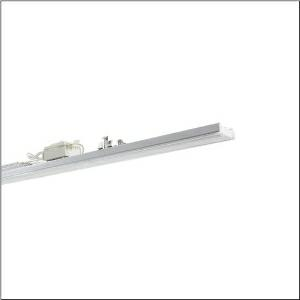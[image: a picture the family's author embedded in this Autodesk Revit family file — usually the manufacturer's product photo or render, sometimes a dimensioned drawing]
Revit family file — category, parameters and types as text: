
# Revit family: licross_r__11_recessed_ho_51tl12dn6d5m_dd4d
name_source: partatom
category: Lighting Fixtures
units: mm (PartAtom-declared; Revit-internal decimal feet)

## family parameters
Cut with Voids When Loaded = No
Host = Face
Light Source = No
Part Type = Normal
Room Calculation Point = No
Round Connector Dimension = Use Diameter
Shared = No

## types (1)
- --- (1 x LED, 13710 lm, 76.8 W, 6500K)
    Apparent Load = 77 VA
    CIE Flux Codes = 66 91 98 100 100
    Color Rendering = 80
    Color Temperature = 6500K
    Default Elevation = 1800 mm
    Description = Licross® 11 Recessed HO, luminaire insert, of sheet steel, coil coated, white, length: 1.500mm, width: 66mm, height: 67mm, LED rated luminous flux: 13.710lm, light colour: 865, control gear: DALI 2, with plug, 5-pole, with phase selection, mains connection: 220..240V, AC, 50/60Hz, rated input power: 77W, internal wiring halogen-free, primary optical cover: cover, of PMMA, light emission: direct distribution, primary light characteristic: symmetric, protection rating (complete): IP40, insulation class (complete): insulation class I (protective earthing), certification: CE, ENEC, VDE, UKCA, protection symbol: D if used in an environment without relevant dust loads with corresponding accessories, impact resistance: IK06, permissible ambient temperature for indoor applications: -25..+30°C, corresponds to IFS (International Featured Standards) requirements for safety and quality in the food industry, reducing of maximum allowable ambient temperature of 5°C with ceiling mounting, LABS conformity tested according to VDMA 24364:2018-05, packaging unit: 1 piece
    Height = 58 mm
    Lamp = 1 x LED
    Lamp Light Flux = 13710 lm
    Lamp Power = 76.8 W
    Lamp count = 1
    Length = 1500 mm
    Luminous efficacy = 179 lm/W
    Manufacturer = Siteco
    ModVariant = No
    Model = 51TL12DN6D5M
    Mounting Place = Ceiling
    Mounting Type = Pendant
    Number of Poles = 1
    OnlyDefault = Yes
    Power Factor = 1
    Product Name = Licross® 11 Recessed HO
    Product group = luminaire insert | ceiling pendant
    ProductGroupID = 902
    Protection Class = Protection class I
    Protection Degree = IP 40
    RLX_Detail_Level = 1
    RLX_Emergency_Light_Flux = 0 lm
    RLX_Emergency_Type = 0
    RLX_Emergency_Type_DB = No
    RlxData = <blob elided: 24585 chars, md5=b61e1a7d>
    Socket = socket
    Standby Power = 0 W
    System Light Flux = 13710 lm
    System Power = 77 W
    Type Comments = factory setting: luminous flux: 100 % | dim-lin: 254 | 522 mA
    Type Image = l_1296930.jpg
    URL = http://relux.com
    VarID = @adj_089063
    Voltage = 0 V
    Weight = 0.00 kg
    Width = 66 mm

## geometry (parser evidence)
native form markers: Blend x4, Sweep x13
no freeform markers — native parametric forms only
